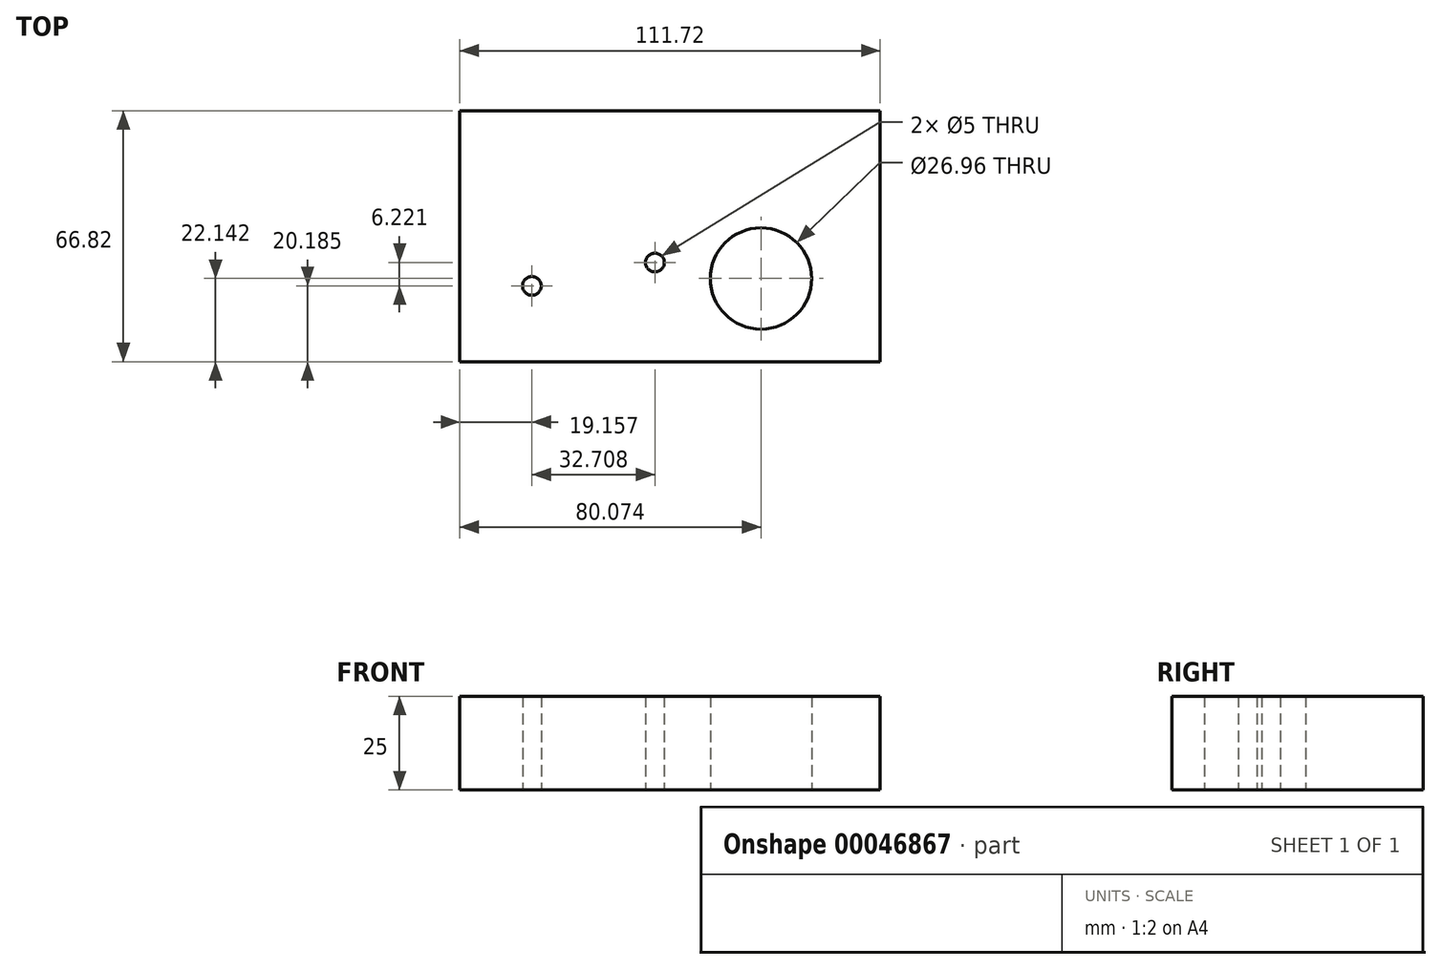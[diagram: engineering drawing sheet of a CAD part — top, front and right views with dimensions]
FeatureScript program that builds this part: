
annotation { "Feature Type Name" : "Feature", "Feature Type Description" : "" }
export const myFeature = defineFeature(function(context is Context, id is Id, definition is map)
    precondition{}
    {
        {
            var Q0;
            Q0=qCreatedBy(makeId("Top.planeOp"),FACE);
            var sketch = newSketch(context, id + "F0", { "sketchPlane" : qUnion([Q0])});
            skLineSegment(sketch, "E0.bottom", {"start": v(-63.21, -13) * mm, "end": v(48.5, -13) * mm});
            skLineSegment(sketch, "E0.top", {"start": v(-63.21, 53.82) * mm, "end": v(48.5, 53.82) * mm});
            skLineSegment(sketch, "E0.left", {"start": v(-63.21, -13) * mm, "end": v(-63.21, 53.82) * mm});
            skLineSegment(sketch, "E0.right", {"start": v(48.5, -13) * mm, "end": v(48.5, 53.82) * mm});
            skPoint(sketch, "E1", {"position": v(-51.86, 0) * mm});
            skPoint(sketch, "E2", {"position": v(-53.9, 40.94) * mm});
            skPoint(sketch, "E3", {"position": v(-17.16, 0) * mm});
            skPoint(sketch, "E4", {"position": v(-21.85, 40.18) * mm});
            skPoint(sketch, "E5", {"position": v(23.7, 0) * mm});
            skPoint(sketch, "E6", {"position": v(23.7, 39.29) * mm});
            skPoint(sketch, "E7", {"position": v(-37.65, 19.5) * mm});
            skSolve(sketch);
        }
        {
            var Q0;
            Q0=makeQuery(id+"F0.imprint","IMPRINT",FACE,{"disambiguationData":[TD([[makeQuery(id+"F0.imprint","IMPRINT",EDGE,{"derivedFrom":sQuery(id+"F0.wireOp",EDGE,"E0.bottom")}),1.0]])]});
            extrude(context, id + "F1", {"entities" : qUnion([Q0]), "depth" : 25 * mm});
        }
        {
            var Q0;
            Q0=qCreatedBy(makeId("Top.planeOp"),FACE);
            var sketch = newSketch(context, id + "F2", { "sketchPlane" : qUnion([Q0])});
            skPoint(sketch, "E8", {"position": v(-44.05, 7.18) * mm});
            skPoint(sketch, "E9", {"position": v(-44.05, 35.83) * mm});
            skPoint(sketch, "E10", {"position": v(-26.8, 0) * mm});
            skPoint(sketch, "E11", {"position": v(-26.8, 34.82) * mm});
            skSolve(sketch);
        }
        {
            var Q0;
            Q0=sQuery(id+"F2.wireOp",VERTEX,"E8");
            var Q1;
            Q1=makeQuery(id+"F1.opExtrude","SWEPT_BODY",BODY,{"disambiguationData":[OSD([sQuery(id+"F0.wireOp",EDGE,"E0.bottom"),sQuery(id+"F0.wireOp",EDGE,"E0.top"),sQuery(id+"F0.wireOp",EDGE,"E0.left"),sQuery(id+"F0.wireOp",EDGE,"E0.right")])]});
            hole(context, id + "F3", {"style" : HoleStyle.SIMPLE, "holeDiameter" : 5 * mm, "endStyle" : HoleEndStyle.THROUGH, "oppositeDirection" : true, "locations" : qUnion([Q0]), "scope" : qUnion([Q1])});
        }
        {
            var Q0;
            Q0=qCreatedBy(makeId("Top.planeOp"),FACE);
            var sketch = newSketch(context, id + "F4", { "sketchPlane" : qUnion([Q0])});
            skCircle(sketch, "E12", {"center": v(-11.35, 13.4) * mm, "radius": 13.9 * mm});
            skSolve(sketch);
        }
        {
            var Q0;
            Q0=sQuery(id+"F4.wireOp",VERTEX,"E12.center");
            var Q1;
            Q1=makeQuery(id+"F1.opExtrude","SWEPT_BODY",BODY,{"disambiguationData":[OSD([sQuery(id+"F0.wireOp",EDGE,"E0.bottom"),sQuery(id+"F0.wireOp",EDGE,"E0.top"),sQuery(id+"F0.wireOp",EDGE,"E0.left"),sQuery(id+"F0.wireOp",EDGE,"E0.right")])]});
            hole(context, id + "F5", {"style" : HoleStyle.SIMPLE, "holeDiameter" : 5 * mm, "endStyle" : HoleEndStyle.THROUGH, "oppositeDirection" : true, "locations" : qUnion([Q0]), "scope" : qUnion([Q1])});
        }
        {
            var Q0;
            Q0=qCreatedBy(makeId("Top.planeOp"),FACE);
            var sketch = newSketch(context, id + "F6", { "sketchPlane" : qUnion([Q0])});
            skCircle(sketch, "E13", {"center": v(16.86, 9.14) * mm, "radius": 13.48 * mm});
            skSolve(sketch);
        }
        {
            var Q0;
            Q0=makeQuery(id+"F6.imprint","IMPRINT",FACE,{"disambiguationData":[TD([[makeQuery(id+"F6.imprint","IMPRINT",EDGE,{"derivedFrom":sQuery(id+"F6.wireOp",EDGE,"E13")}),1.0]])]});
            extrude(context, id + "F7", {"entities" : qUnion([Q0]), "operationType" : NewBodyOperationType.REMOVE, "endBound" : BoundingType.THROUGH_ALL, "depth" : 25 * mm});
        }
    });
